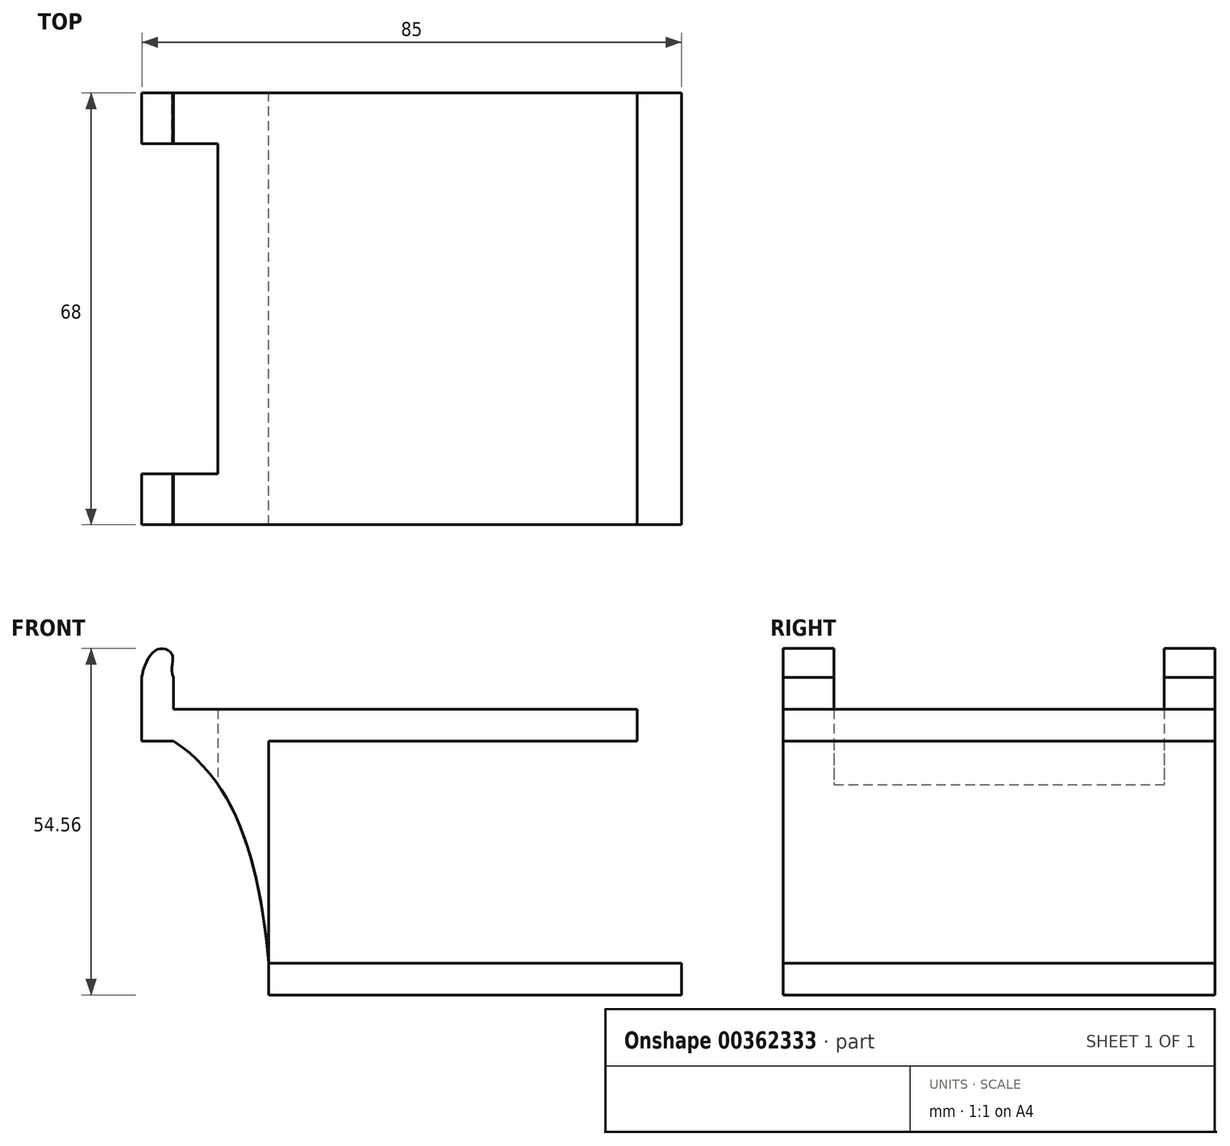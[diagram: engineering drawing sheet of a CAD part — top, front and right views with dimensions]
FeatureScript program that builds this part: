
annotation { "Feature Type Name" : "Feature", "Feature Type Description" : "" }
export const myFeature = defineFeature(function(context is Context, id is Id, definition is map)
    precondition{}
    {
        {
            var Q0;
            Q0=qCreatedBy(makeId("Front.planeOp"),FACE);
            var sketch = newSketch(context, id + "F0", { "sketchPlane" : qUnion([Q0])});
            skLineSegment(sketch, "E0.bottom", {"start": v(30.68, 0) * mm, "end": v(-27.32, 0) * mm});
            skLineSegment(sketch, "E0.top", {"start": v(30.68, 5) * mm, "end": v(-27.32, 5) * mm});
            skLineSegment(sketch, "E0.left", {"start": v(30.68, 0) * mm, "end": v(30.68, 5) * mm});
            skLineSegment(sketch, "E0.right", {"start": v(-27.32, 0) * mm, "end": v(-27.32, 5) * mm});
            skLineSegment(sketch, "E1.bottom", {"start": v(-27.32, 0) * mm, "end": v(-22.32, 0) * mm});
            skLineSegment(sketch, "E1.top", {"start": v(-27.32, -35) * mm, "end": v(-22.32, -35) * mm});
            skLineSegment(sketch, "E1.left", {"start": v(-27.32, 0) * mm, "end": v(-27.32, -35) * mm});
            skLineSegment(sketch, "E1.right", {"start": v(-22.32, 0) * mm, "end": v(-22.32, -35) * mm});
            skLineSegment(sketch, "E2.bottom", {"start": v(-27.32, -35) * mm, "end": v(37.68, -35) * mm});
            skLineSegment(sketch, "E2.top", {"start": v(-27.32, -40) * mm, "end": v(37.68, -40) * mm});
            skLineSegment(sketch, "E2.left", {"start": v(-27.32, -35) * mm, "end": v(-27.32, -40) * mm});
            skLineSegment(sketch, "E2.right", {"start": v(37.68, -35) * mm, "end": v(37.68, -40) * mm});
            skLineSegment(sketch, "E3.bottom", {"start": v(-27.32, 5) * mm, "end": v(-42.32, 5) * mm});
            skLineSegment(sketch, "E3.top", {"start": v(-27.32, 0) * mm, "end": v(-42.32, 0) * mm});
            skLineSegment(sketch, "E3.left", {"start": v(-27.32, 5) * mm, "end": v(-27.32, 0) * mm});
            skLineSegment(sketch, "E3.right", {"start": v(-42.32, 5) * mm, "end": v(-42.32, 0) * mm});
            skFitSpline(sketch, "E4", {"points": [v(-42.32, 0) * mm, v(-27.32, -35) * mm], "startDerivative": vector(30.42, -19.78) * mm, "endDerivative": vector(4.3, -46.23) * mm});
            skSolve(sketch);
        }
        {
            var Q0;
            Q0=makeQuery(id+"F0.imprint","IMPRINT",FACE,{"disambiguationData":[TD([[makeQuery(id+"F0.imprint","IMPRINT",EDGE,{"derivedFrom":sQuery(id+"F0.wireOp",EDGE,"E0.bottom")}),-1.0]])]});
            var Q1;
            Q1=makeQuery(id+"F0.imprint","IMPRINT",FACE,{"disambiguationData":[TD([[makeQuery(id+"F0.imprint","IMPRINT",EDGE,{"derivedFrom":sQuery(id+"F0.wireOp",EDGE,"E3.bottom")}),1.0]])]});
            var Q2;
            Q2=makeQuery(id+"F0.imprint","IMPRINT",FACE,{"disambiguationData":[TD([[makeQuery(id+"F0.imprint","IMPRINT",EDGE,{"derivedFrom":sQuery(id+"F0.wireOp",EDGE,"E1.left")}),-1.0]])]});
            var Q3;
            Q3=makeQuery(id+"F0.imprint","IMPRINT",FACE,{"disambiguationData":[TD([[makeQuery(id+"F0.imprint","IMPRINT",EDGE,{"derivedFrom":sQuery(id+"F0.wireOp",EDGE,"E1.bottom")}),-1.0]])]});
            var Q4;
            Q4=makeQuery(id+"F0.imprint","IMPRINT",FACE,{"disambiguationData":[TD([[makeQuery(id+"F0.imprint","IMPRINT",EDGE,{"derivedFrom":sQuery(id+"F0.wireOp",EDGE,"E2.top")}),1.0]])]});
            extrude(context, id + "F1", {"entities" : qUnion([Q0, Q1, Q2, Q3, Q4]), "endBound" : BoundingType.SYMMETRIC, "depth" : 68 * mm});
        }
        {
            var Q0;
            Q0=qCreatedBy(makeId("Front.planeOp"),FACE);
            var sketch = newSketch(context, id + "F2", { "sketchPlane" : qUnion([Q0])});
            skLineSegment(sketch, "E5.bottom", {"start": v(-42.32, 0) * mm, "end": v(-47.32, 0) * mm});
            skLineSegment(sketch, "E5.top", {"start": v(-42.32, 10) * mm, "end": v(-47.32, 10) * mm});
            skLineSegment(sketch, "E5.left", {"start": v(-42.32, 0) * mm, "end": v(-42.32, 10) * mm});
            skLineSegment(sketch, "E5.right", {"start": v(-47.32, 0) * mm, "end": v(-47.32, 10) * mm});
            skFitSpline(sketch, "E6", {"points": [v(-47.32, 10) * mm, v(-44.74, 14.46) * mm, v(-42.55, 13.6) * mm, v(-42.32, 10) * mm], "startDerivative": vector(1.51, 14) * mm, "endDerivative": vector(5.42, -12.6) * mm});
            skSolve(sketch);
        }
        {
            var Q0;
            Q0=makeQuery(id+"F2.imprint","IMPRINT",FACE,{"disambiguationData":[TD([[makeQuery(id+"F2.imprint","IMPRINT",EDGE,{"derivedFrom":sQuery(id+"F2.wireOp",EDGE,"E5.bottom")}),-1.0]])]});
            var Q1;
            Q1=makeQuery(id+"F2.imprint","IMPRINT",FACE,{"disambiguationData":[TD([[makeQuery(id+"F2.imprint","IMPRINT",EDGE,{"derivedFrom":sQuery(id+"F2.wireOp",EDGE,"E5.top")}),-1.0]])]});
            var Q2;
            Q2=makeQuery(id+"F1.opExtrude","CAP_FACE",FACE,{"disambiguationData":[OSD([sQuery(id+"F0.wireOp",EDGE,"E0.bottom"),sQuery(id+"F0.wireOp",EDGE,"E0.top"),sQuery(id+"F0.wireOp",EDGE,"E0.left"),sQuery(id+"F0.wireOp",EDGE,"E1.right"),sQuery(id+"F0.wireOp",EDGE,"E2.bottom"),sQuery(id+"F0.wireOp",EDGE,"E2.top"),sQuery(id+"F0.wireOp",EDGE,"E2.left"),sQuery(id+"F0.wireOp",EDGE,"E2.right"),sQuery(id+"F0.wireOp",EDGE,"E3.bottom"),sQuery(id+"F0.wireOp",EDGE,"E3.right"),sQuery(id+"F0.wireOp",EDGE,"E4")])],"isStart":false});
            extrude(context, id + "F3", {"entities" : qUnion([Q0, Q1]), "operationType" : NewBodyOperationType.ADD, "endBound" : BoundingType.SYMMETRIC, "endBoundEntityFace" : qUnion([Q2]), "depth" : 68 * mm});
        }
        {
            var Q0;
            Q0=qCreatedBy(makeId("Front.planeOp"),FACE);
            var sketch = newSketch(context, id + "F4", { "sketchPlane" : qUnion([Q0])});
            skLineSegment(sketch, "E7.bottom", {"start": v(-51.58, 21.76) * mm, "end": v(-35.32, 21.76) * mm});
            skLineSegment(sketch, "E7.top", {"start": v(-51.58, -20.97) * mm, "end": v(-35.32, -20.97) * mm});
            skLineSegment(sketch, "E7.left", {"start": v(-51.58, 21.76) * mm, "end": v(-51.58, -20.97) * mm});
            skLineSegment(sketch, "E7.right", {"start": v(-35.32, 21.76) * mm, "end": v(-35.32, -20.97) * mm});
            skSolve(sketch);
        }
        {
            var Q0;
            Q0=makeQuery(id+"F4.imprint","IMPRINT",FACE,{"disambiguationData":[TD([[makeQuery(id+"F4.imprint","IMPRINT",EDGE,{"derivedFrom":sQuery(id+"F4.wireOp",EDGE,"E7.bottom")}),-1.0]])]});
            extrude(context, id + "F5", {"entities" : qUnion([Q0]), "operationType" : NewBodyOperationType.REMOVE, "endBound" : BoundingType.SYMMETRIC, "depth" : 52 * mm});
        }
    });
